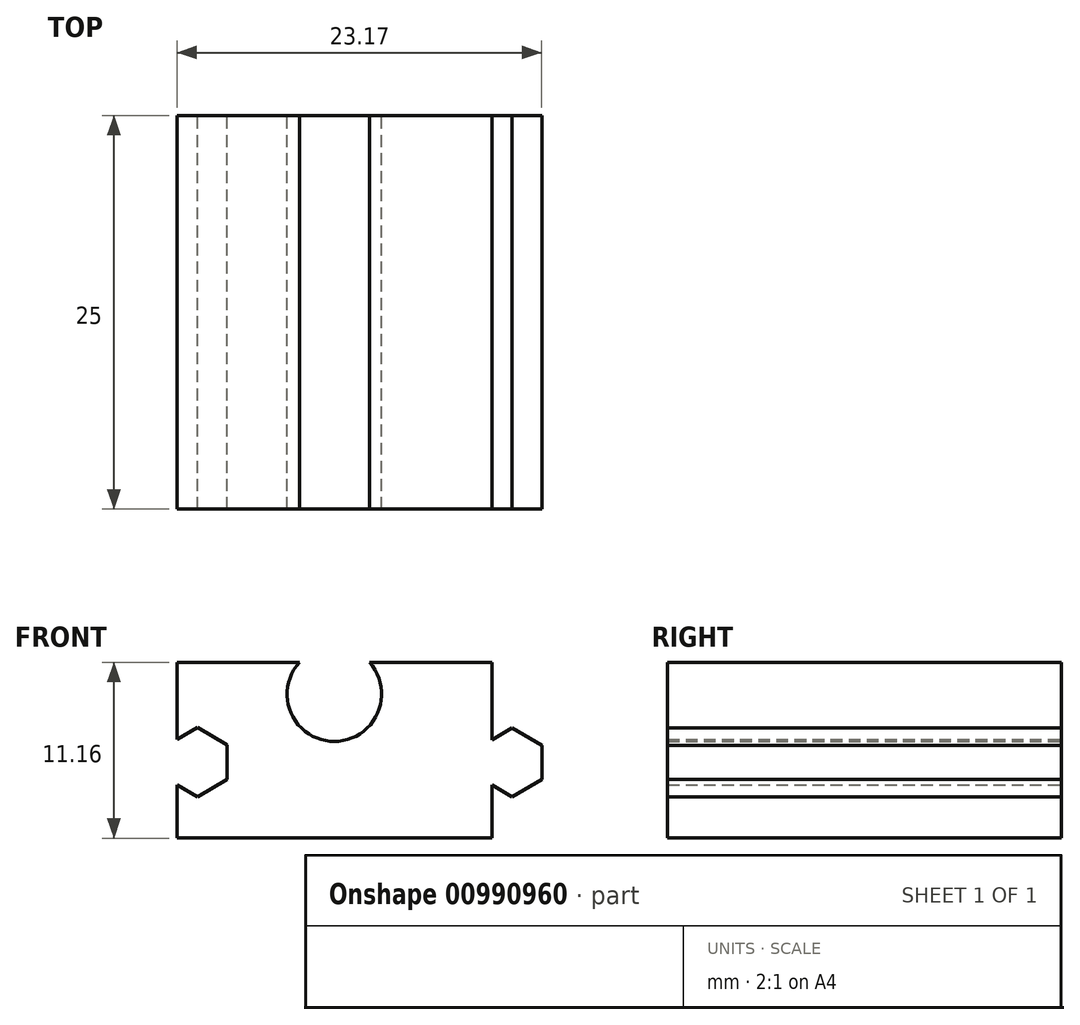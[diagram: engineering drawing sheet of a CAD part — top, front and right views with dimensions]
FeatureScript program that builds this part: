
annotation { "Feature Type Name" : "Feature", "Feature Type Description" : "" }
export const myFeature = defineFeature(function(context is Context, id is Id, definition is map)
    precondition{}
    {
        {
            var Q0;
            Q0=qCreatedBy(makeId("Front.planeOp"),FACE);
            var sketch = newSketch(context, id + "F0", { "sketchPlane" : qUnion([Q0])});
            skLineSegment(sketch, "E0.bottom", {"start": v(10, -5.58) * mm, "end": v(-10, -5.58) * mm});
            skLineSegment(sketch, "E0.top", {"start": v(10, 5.58) * mm, "end": v(-10, 5.58) * mm});
            skLineSegment(sketch, "E0.left", {"start": v(10, -5.58) * mm, "end": v(10, 5.58) * mm});
            skLineSegment(sketch, "E0.right", {"start": v(-10, -5.58) * mm, "end": v(-10, 5.58) * mm});
            skPoint(sketch, "E0.middle", {"position": v(0, 0) * mm});
            skPoint(sketch, "E1", {"position": v(0.02, -0.77) * mm});
            skPoint(sketch, "E2", {"position": v(0, 3.56) * mm});
            skCircle(sketch, "E3", {"center": v(0, 3.56) * mm, "radius": 3 * mm});
            skLineSegment(sketch, "E4", {"start": v(0.02, -0.77) * mm, "end": v(-15.54, -0.77) * mm, "construction": true});
            skLineSegment(sketch, "E5", {"start": v(0, 0) * mm, "end": v(-12.37, 0) * mm, "construction": true});
            skLineSegment(sketch, "E6", {"start": v(0, 13.33) * mm, "end": v(0, -12.08) * mm, "construction": true});
            skLineSegment(sketch, "E7.MirrorCS", {"start": v(0, 0) * mm, "end": v(12.37, 0) * mm, "construction": true});
            skLineSegment(sketch, "E8.MirrorCS", {"start": v(-0.02, -0.77) * mm, "end": v(15.54, -0.77) * mm, "construction": true});
            skCircle(sketch, "E9.cCircle", {"center": v(-8.7, -0.75) * mm, "radius": 1.9 * mm, "construction": true});
            skLineSegment(sketch, "E9.0", {"start": v(-6.8, -1.85) * mm, "end": v(-8.7, -2.95) * mm});
            skLineSegment(sketch, "E9.1", {"start": v(-8.7, -2.95) * mm, "end": v(-10.6, -1.85) * mm});
            skLineSegment(sketch, "E9.2", {"start": v(-10.6, -1.85) * mm, "end": v(-10.6, 0.34) * mm});
            skLineSegment(sketch, "E9.3", {"start": v(-10.6, 0.34) * mm, "end": v(-8.7, 1.44) * mm});
            skLineSegment(sketch, "E9.4", {"start": v(-8.7, 1.44) * mm, "end": v(-6.8, 0.34) * mm});
            skLineSegment(sketch, "E9.5", {"start": v(-6.8, 0.34) * mm, "end": v(-6.8, -1.85) * mm});
            skPoint(sketch, "E9.0.midPoint", {"position": v(-7.75, -2.4) * mm});
            skCircle(sketch, "E10.cCircle", {"center": v(11.29, -0.77) * mm, "radius": 1.89 * mm, "construction": true});
            skLineSegment(sketch, "E10.0", {"start": v(13.17, -1.85) * mm, "end": v(11.29, -2.94) * mm});
            skLineSegment(sketch, "E10.1", {"start": v(11.29, -2.94) * mm, "end": v(9.4, -1.85) * mm});
            skLineSegment(sketch, "E10.2", {"start": v(9.4, -1.85) * mm, "end": v(9.4, 0.32) * mm});
            skLineSegment(sketch, "E10.3", {"start": v(9.4, 0.32) * mm, "end": v(11.29, 1.41) * mm});
            skLineSegment(sketch, "E10.4", {"start": v(11.29, 1.41) * mm, "end": v(13.17, 0.32) * mm});
            skLineSegment(sketch, "E10.5", {"start": v(13.17, 0.32) * mm, "end": v(13.17, -1.85) * mm});
            skPoint(sketch, "E10.0.midPoint", {"position": v(12.23, -2.4) * mm});
            skSolve(sketch);
        }
        {
            var Q0;
            {var subQ0=sQuery(id+"F0.wireOp",EDGE,"5b1f0303-7e19-4a52-9026-6a9802054e040.MirrorCS");Q0=makeQuery(id+"F0.imprint","IMPRINT",FACE,{"disambiguationData":[TD([[makeQuery(id+"F0.imprint","IMPRINT",EDGE,{"derivedFrom":subQ0}),1.0]])]});}
            var Q1;
            {var subQ0=sQuery(id+"F0.wireOp",EDGE,"cc34c8df-07c0-4cc4-8682-5ab28225645b0.MirrorCS");Q1=makeQuery(id+"F0.imprint","IMPRINT",FACE,{"disambiguationData":[TD([[makeQuery(id+"F0.imprint","IMPRINT",EDGE,{"derivedFrom":subQ0}),1.0]])]});}
            var Q2;
            {var subQ1=sQuery(id+"F0.wireOp",EDGE,"474448f5-d81b-42c5-8d5d-bf9c72034bf10.MirrorCS");Q2=makeQuery(id+"F0.imprint","IMPRINT",FACE,{"disambiguationData":[TD([[makeQuery(id+"F0.imprint","IMPRINT",EDGE,{"derivedFrom":subQ1}),-1.0]])]});}
            var Q3;
            {var subQ9=sQuery(id+"F0.wireOp",EDGE,"E0.bottom");Q3=makeQuery(id+"F0.imprint","IMPRINT",FACE,{"disambiguationData":[TD([[makeQuery(id+"F0.imprint","IMPRINT",EDGE,{"derivedFrom":subQ9}),-1.0]])]});}
            var Q4;
            {var subQ0=sQuery(id+"F0.wireOp",EDGE,"a87e99a6-b751-4f87-851f-dcfc72f002b5");Q4=makeQuery(id+"F0.imprint","IMPRINT",FACE,{"disambiguationData":[TD([[makeQuery(id+"F0.imprint","IMPRINT",EDGE,{"derivedFrom":subQ0}),-1.0]])]});}
            var Q5;
            {var subQ1=sQuery(id+"F0.wireOp",EDGE,"E10.0");Q5=makeQuery(id+"F0.imprint","IMPRINT",FACE,{"disambiguationData":[TD([[makeQuery(id+"F0.imprint","IMPRINT",EDGE,{"derivedFrom":subQ1}),-1.0]])]});}
            var Q6;
            {var subQ5=sQuery(id+"F0.wireOp",EDGE,"E10.2");Q6=makeQuery(id+"F0.imprint","IMPRINT",FACE,{"disambiguationData":[TD([[makeQuery(id+"F0.imprint","IMPRINT",EDGE,{"derivedFrom":subQ5}),-1.0]])]});}
            extrude(context, id + "F1", {"entities" : qUnion([Q0, Q1, Q2, Q3, Q4, Q5, Q6]), "depth" : 25 * mm, "offsetDistance" : 25 * mm});
        }
    });
